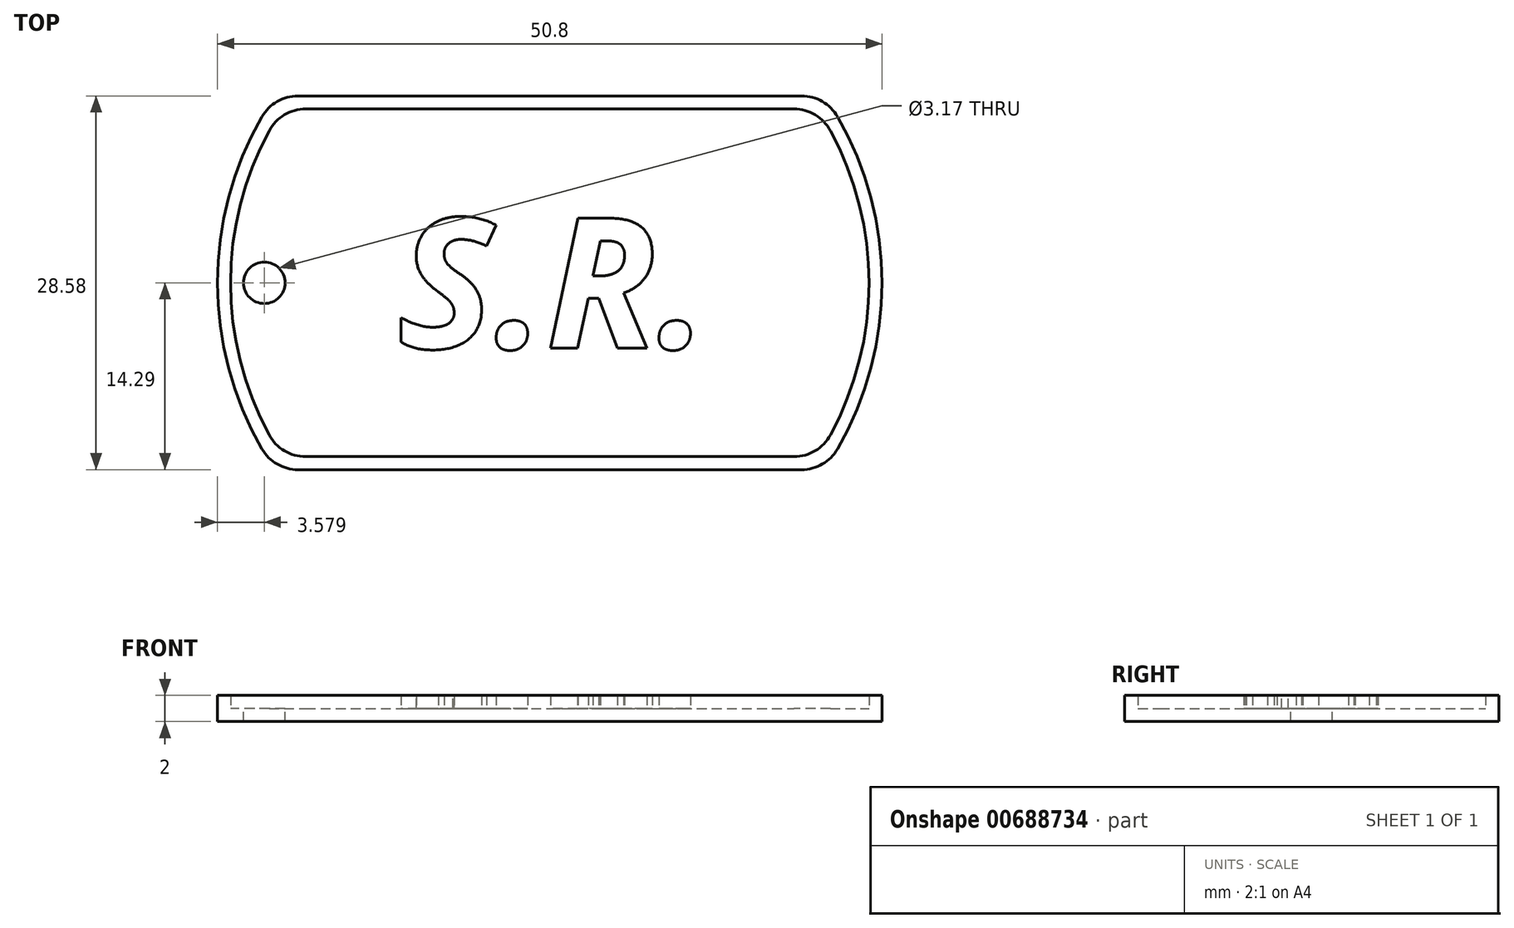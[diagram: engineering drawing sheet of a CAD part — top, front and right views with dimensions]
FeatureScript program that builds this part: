
annotation { "Feature Type Name" : "Feature", "Feature Type Description" : "" }
export const myFeature = defineFeature(function(context is Context, id is Id, definition is map)
    precondition{}
    {
        {
            var Q0;
            Q0=qCreatedBy(makeId("Top.planeOp"),FACE);
            var sketch = newSketch(context, id + "F0", { "sketchPlane" : qUnion([Q0])});
            skArc(sketch, "E0", {"start": v(-22, 12.7) * mm, "mid": v(-25.4, 0) * mm, "end": v(-22, -12.7) * mm});
            skLineSegment(sketch, "E1.top", {"start": v(-19.25, -14.29) * mm, "end": v(19.25, -14.29) * mm});
            skArc(sketch, "E2.trimOffspring", {"start": v(22, -12.7) * mm, "mid": v(25.4, 0) * mm, "end": v(22, 12.7) * mm});
            skLineSegment(sketch, "E3", {"start": v(-19.25, 14.29) * mm, "end": v(19.25, 14.29) * mm});
            skPoint(sketch, "E4.visualSharp", {"position": v(-21, 14.29) * mm});
            skArc(sketch, "E4.filletArc", {"start": v(-19.25, 14.29) * mm, "mid": v(-20.83, 13.86) * mm, "end": v(-22, 12.7) * mm});
            skPoint(sketch, "E5.visualSharp", {"position": v(21, 14.29) * mm});
            skArc(sketch, "E5.filletArc", {"start": v(22, 12.7) * mm, "mid": v(20.83, 13.86) * mm, "end": v(19.25, 14.29) * mm});
            skPoint(sketch, "E6.visualSharp", {"position": v(21, -14.29) * mm});
            skArc(sketch, "E6.filletArc", {"start": v(19.25, -14.29) * mm, "mid": v(20.83, -13.86) * mm, "end": v(22, -12.7) * mm});
            skPoint(sketch, "E7.visualSharp", {"position": v(-21, -14.29) * mm});
            skArc(sketch, "E7.filletArc", {"start": v(-22, -12.7) * mm, "mid": v(-20.83, -13.86) * mm, "end": v(-19.25, -14.29) * mm});
            skSolve(sketch);
        }
        {
            var Q0;
            Q0=makeQuery(id+"F0.imprint","IMPRINT",FACE,{"disambiguationData":[TD([[makeQuery(id+"F0.imprint","IMPRINT",EDGE,{"derivedFrom":sQuery(id+"F0.wireOp",EDGE,"E0")}),1.0]])]});
            extrude(context, id + "F1", {"entities" : qUnion([Q0]), "depth" : 1 * mm, "offsetDistance" : 25.4 * mm});
        }
        {
            var Q0;
            Q0=makeQuery(id+"F1.opExtrude","CAP_FACE",FACE,{"disambiguationData":[OSD([sQuery(id+"F0.wireOp",EDGE,"E0"),sQuery(id+"F0.wireOp",EDGE,"E1.top"),sQuery(id+"F0.wireOp",EDGE,"E2.trimOffspring"),sQuery(id+"F0.wireOp",EDGE,"E3"),sQuery(id+"F0.wireOp",EDGE,"E4.filletArc"),sQuery(id+"F0.wireOp",EDGE,"E5.filletArc"),sQuery(id+"F0.wireOp",EDGE,"E6.filletArc"),sQuery(id+"F0.wireOp",EDGE,"E7.filletArc")])],"isStart":false});
            var sketch = newSketch(context, id + "F2", { "sketchPlane" : qUnion([Q0])});
            skLineSegment(sketch, "E8.0", {"start": v(-18.66, 13.29) * mm, "end": v(18.66, 13.29) * mm});
            skArc(sketch, "E8.1", {"start": v(-21.45, 11.63) * mm, "mid": v(-24.4, 0) * mm, "end": v(-21.45, -11.63) * mm});
            skLineSegment(sketch, "E8.2", {"start": v(-18.66, -13.29) * mm, "end": v(18.66, -13.29) * mm});
            skArc(sketch, "E8.3", {"start": v(21.45, -11.63) * mm, "mid": v(24.4, 0) * mm, "end": v(21.45, 11.63) * mm});
            skPoint(sketch, "E9.visualSharp", {"position": v(-20.46, 13.29) * mm});
            skArc(sketch, "E9.filletArc", {"start": v(-18.66, 13.29) * mm, "mid": v(-20.29, 12.84) * mm, "end": v(-21.45, 11.63) * mm});
            skPoint(sketch, "E10.visualSharp", {"position": v(20.46, 13.29) * mm});
            skArc(sketch, "E10.filletArc", {"start": v(21.45, 11.63) * mm, "mid": v(20.29, 12.84) * mm, "end": v(18.66, 13.29) * mm});
            skPoint(sketch, "E11.visualSharp", {"position": v(20.46, -13.29) * mm});
            skArc(sketch, "E11.filletArc", {"start": v(18.66, -13.29) * mm, "mid": v(20.29, -12.84) * mm, "end": v(21.45, -11.63) * mm});
            skPoint(sketch, "E12.visualSharp", {"position": v(-20.46, -13.29) * mm});
            skArc(sketch, "E12.filletArc", {"start": v(-21.45, -11.63) * mm, "mid": v(-20.29, -12.84) * mm, "end": v(-18.66, -13.29) * mm});
            skLineSegment(sketch, "E13.0", {"start": v(-19.25, 14.29) * mm, "end": v(19.25, 14.29) * mm});
            skArc(sketch, "E13.1", {"start": v(-22, 12.7) * mm, "mid": v(-25.4, 0) * mm, "end": v(-22, -12.7) * mm});
            skLineSegment(sketch, "E13.2", {"start": v(-19.25, -14.29) * mm, "end": v(19.25, -14.29) * mm});
            skArc(sketch, "E13.3", {"start": v(22, -12.7) * mm, "mid": v(25.4, 0) * mm, "end": v(22, 12.7) * mm});
            skPoint(sketch, "E14.visualSharp", {"position": v(-21, -14.29) * mm});
            skArc(sketch, "E14.filletArc", {"start": v(-22, -12.7) * mm, "mid": v(-20.83, -13.86) * mm, "end": v(-19.25, -14.29) * mm});
            skPoint(sketch, "E15.visualSharp", {"position": v(21, -14.29) * mm});
            skArc(sketch, "E15.filletArc", {"start": v(19.25, -14.29) * mm, "mid": v(20.83, -13.86) * mm, "end": v(22, -12.7) * mm});
            skPoint(sketch, "E16.visualSharp", {"position": v(21, 14.29) * mm});
            skArc(sketch, "E16.filletArc", {"start": v(22, 12.7) * mm, "mid": v(20.83, 13.86) * mm, "end": v(19.25, 14.29) * mm});
            skPoint(sketch, "E17.visualSharp", {"position": v(-21, 14.29) * mm});
            skArc(sketch, "E17.filletArc", {"start": v(-19.25, 14.29) * mm, "mid": v(-20.83, 13.86) * mm, "end": v(-22, 12.7) * mm});
            skSolve(sketch);
        }
        {
            var Q0;
            Q0=makeQuery(id+"F2.imprint","IMPRINT",FACE,{"disambiguationData":[TD([[makeQuery(id+"F2.imprint","IMPRINT",EDGE,{"derivedFrom":sQuery(id+"F2.wireOp",EDGE,"E8.0")}),1.0]])]});
            extrude(context, id + "F3", {"entities" : qUnion([Q0]), "operationType" : NewBodyOperationType.ADD, "depth" : 1 * mm, "offsetDistance" : 25.4 * mm});
        }
        {
            var Q0;
            Q0=makeQuery(id+"F1.opExtrude","CAP_FACE",FACE,{"disambiguationData":[OSD([sQuery(id+"F0.wireOp",EDGE,"E0"),sQuery(id+"F0.wireOp",EDGE,"E1.top"),sQuery(id+"F0.wireOp",EDGE,"E2.trimOffspring"),sQuery(id+"F0.wireOp",EDGE,"E3"),sQuery(id+"F0.wireOp",EDGE,"E4.filletArc"),sQuery(id+"F0.wireOp",EDGE,"E5.filletArc"),sQuery(id+"F0.wireOp",EDGE,"E6.filletArc"),sQuery(id+"F0.wireOp",EDGE,"E7.filletArc")])],"isStart":false});
            var sketch = newSketch(context, id + "F4", { "sketchPlane" : qUnion([Q0])});
            skCircle(sketch, "E18", {"center": v(-21.82, 0) * mm, "radius": 1.59 * mm});
            skSolve(sketch);
        }
        {
            var Q0;
            Q0=makeQuery(id+"F4.imprint","IMPRINT",FACE,{"disambiguationData":[TD([[makeQuery(id+"F4.imprint","IMPRINT",EDGE,{"derivedFrom":sQuery(id+"F4.wireOp",EDGE,"E18")}),1.0]])]});
            extrude(context, id + "F5", {"entities" : qUnion([Q0]), "operationType" : NewBodyOperationType.REMOVE, "oppositeDirection" : true, "depth" : 1 * mm, "offsetDistance" : 25.4 * mm});
        }
        {
            var Q0;
            Q0=makeQuery(id+"F1.opExtrude","CAP_FACE",FACE,{"disambiguationData":[OSD([sQuery(id+"F0.wireOp",EDGE,"E0"),sQuery(id+"F0.wireOp",EDGE,"E1.top"),sQuery(id+"F0.wireOp",EDGE,"E2.trimOffspring"),sQuery(id+"F0.wireOp",EDGE,"E3"),sQuery(id+"F0.wireOp",EDGE,"E4.filletArc"),sQuery(id+"F0.wireOp",EDGE,"E5.filletArc"),sQuery(id+"F0.wireOp",EDGE,"E6.filletArc"),sQuery(id+"F0.wireOp",EDGE,"E7.filletArc")])],"isStart":false});
            var sketch = newSketch(context, id + "F6", { "sketchPlane" : qUnion([Q0])});
            skText(sketch, "E19", { "text": "S.R.", "fontName": "OpenSans-BoldItalic.ttf"});
            const initialGuessF6  = {"E19": [-0.01164, -0.005, 1, 0, 0.01002]};
            skSetInitialGuess(sketch, initialGuessF6);
            skSolve(sketch);
        }
        {
            var Q0;
            Q0 = qSketchRegion(id + "F6", true);
            extrude(context, id + "F7", {"entities" : qUnion([Q0]), "operationType" : NewBodyOperationType.ADD, "depth" : 1 * mm, "offsetDistance" : 25.4 * mm});
        }
    });
